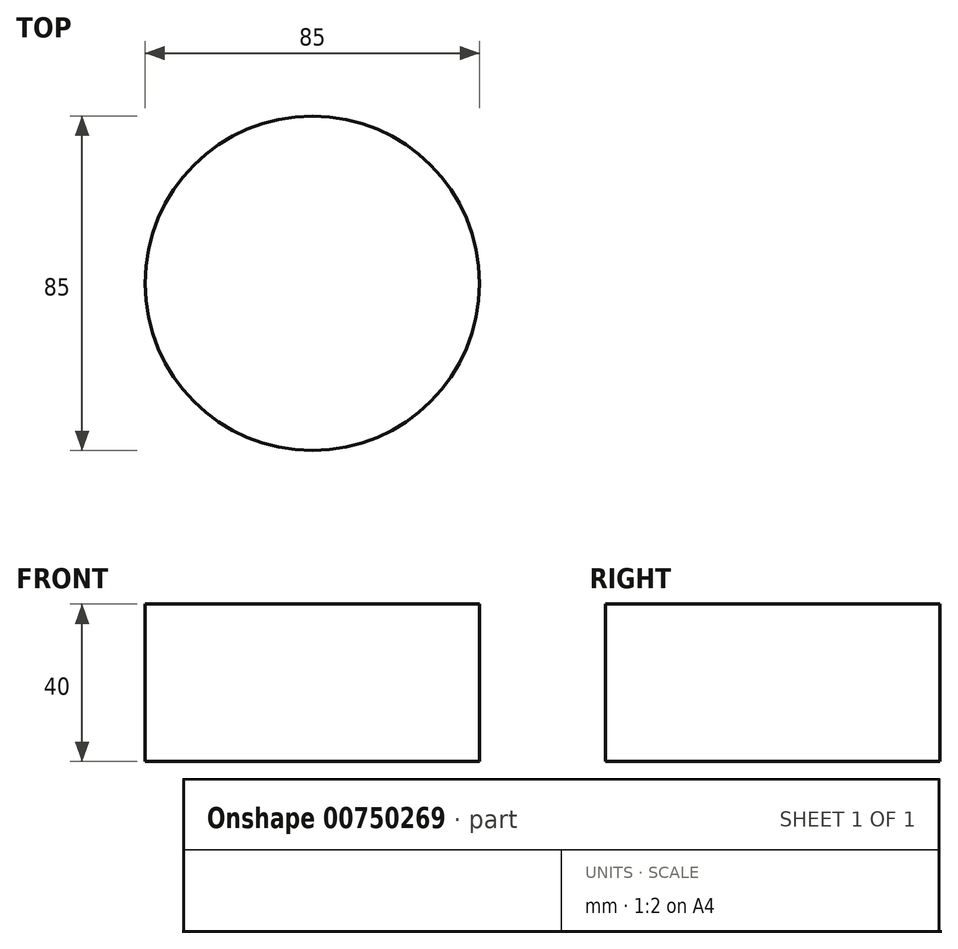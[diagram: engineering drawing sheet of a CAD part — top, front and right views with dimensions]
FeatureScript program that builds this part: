
annotation { "Feature Type Name" : "Feature", "Feature Type Description" : "" }
export const myFeature = defineFeature(function(context is Context, id is Id, definition is map)
    precondition{}
    {
        {
            var Q0;
            Q0=qCreatedBy(makeId("Top.planeOp"),FACE);
            var sketch = newSketch(context, id + "F0", { "sketchPlane" : qUnion([Q0])});
            skCircle(sketch, "E0", {"center": v(0, 0) * mm, "radius": 42.5 * mm});
            skSolve(sketch);
        }
        {
            var Q0;
            Q0=makeQuery(id+"F0.imprint","IMPRINT",FACE,{"disambiguationData":[TD([[makeQuery(id+"F0.imprint","IMPRINT",EDGE,{"derivedFrom":sQuery(id+"F0.wireOp",EDGE,"E0")}),1.0]])]});
            extrude(context, id + "F1", {"entities" : qUnion([Q0]), "flatOperationType" : FlatOperationType.REMOVE, "depth" : 40 * mm, "offsetDistance" : 25 * mm, "domain" : OperationDomain.MODEL});
        }
    });
